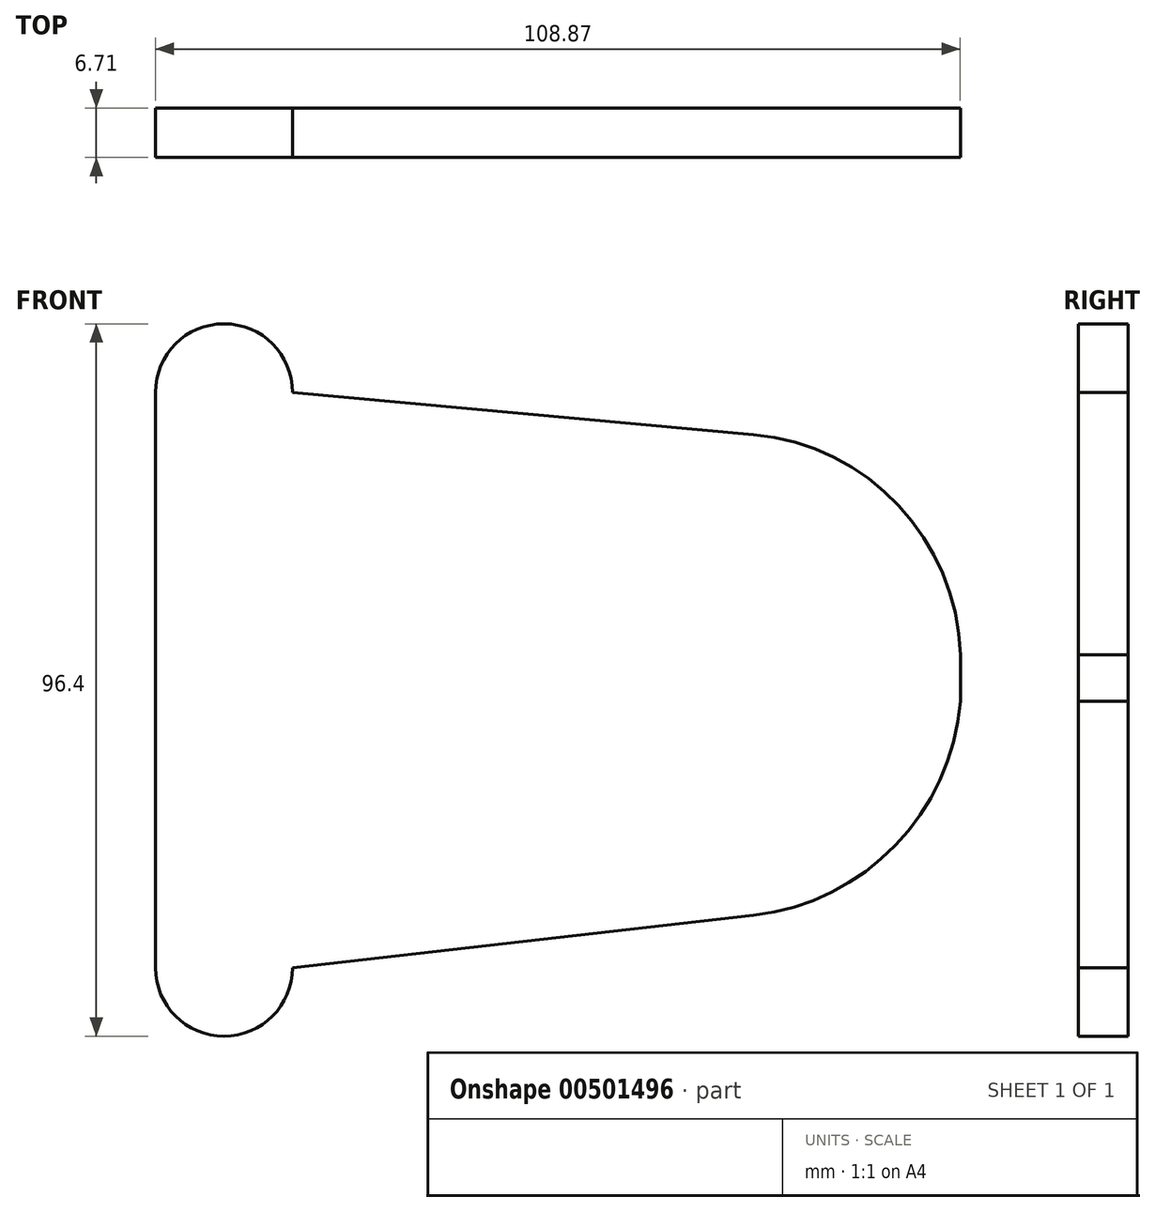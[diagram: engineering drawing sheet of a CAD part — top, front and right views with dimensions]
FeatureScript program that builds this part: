
annotation { "Feature Type Name" : "Feature", "Feature Type Description" : "" }
export const myFeature = defineFeature(function(context is Context, id is Id, definition is map)
    precondition{}
    {
        {
            var Q0;
            Q0=qCreatedBy(makeId("Front.planeOp"),FACE);
            var sketch = newSketch(context, id + "F0", { "sketchPlane" : qUnion([Q0])});
            skLineSegment(sketch, "E0.left", {"start": v(-50.55, 38.87) * mm, "end": v(-50.55, -39) * mm});
            skLineSegment(sketch, "E1", {"start": v(-32, -39) * mm, "end": v(30.35, -31.92) * mm});
            skLineSegment(sketch, "E2", {"start": v(-32, 38.87) * mm, "end": v(30.35, 33.14) * mm});
            skArc(sketch, "E3", {"start": v(-32, 38.87) * mm, "mid": v(-41.28, 48.14) * mm, "end": v(-50.55, 38.87) * mm});
            skArc(sketch, "E4", {"start": v(-32, -39) * mm, "mid": v(-41.28, -48.26) * mm, "end": v(-50.55, -39) * mm});
            skArc(sketch, "E5", {"start": v(30.35, 33.14) * mm, "mid": v(50, 23.54) * mm, "end": v(58.32, 3.34) * mm});
            skArc(sketch, "E6", {"start": v(30.35, -31.92) * mm, "mid": v(49.53, -22.47) * mm, "end": v(58.32, -2.97) * mm});
            skLineSegment(sketch, "E7", {"start": v(58.32, -2.97) * mm, "end": v(58.32, 3.34) * mm});
            skSolve(sketch);
        }
        {
            var Q0;
            Q0=makeQuery(id+"F0.imprint","IMPRINT",FACE,{"disambiguationData":[TD([[makeQuery(id+"F0.imprint","IMPRINT",EDGE,{"derivedFrom":sQuery(id+"F0.wireOp",EDGE,"E0.left")}),1.0]])]});
            extrude(context, id + "F1", {"entities" : qUnion([Q0]), "depth" : 6.7 * mm});
        }
        {
            var Q0;
            Q0=qCreatedBy(makeId("Front.planeOp"),FACE);
            var sketch = newSketch(context, id + "F2", { "sketchPlane" : qUnion([Q0])});
            skCircle(sketch, "E8", {"center": v(-39.08, 28.93) * mm, "radius": 6.72 * mm});
            skCircle(sketch, "E9", {"center": v(-39.08, -27.54) * mm, "radius": 6.72 * mm});
            skSolve(sketch);
        }
        {
            var Q0;
            Q0=sQuery(id+"F2.wireOp",EDGE,"E8");
            var Q1;
            Q1=sQuery(id+"F2.wireOp",EDGE,"E9");
            extrude(context, id + "F3", {"bodyType" : ToolBodyType.SURFACE, "surfaceEntities" : qUnion([Q0, Q1]), "depth" : 30.48 * mm});
        }
        {
            var Q0;
            Q0=qCreatedBy(makeId("Front.planeOp"),FACE);
            var sketch = newSketch(context, id + "F4", { "sketchPlane" : qUnion([Q0])});
            skLineSegment(sketch, "E10.bottom", {"start": v(15.26, 20.7) * mm, "end": v(41.8, 20.7) * mm});
            skLineSegment(sketch, "E10.top", {"start": v(15.26, -17.17) * mm, "end": v(41.8, -17.17) * mm});
            skLineSegment(sketch, "E10.left", {"start": v(15.26, 20.7) * mm, "end": v(15.26, -17.17) * mm});
            skLineSegment(sketch, "E10.right", {"start": v(41.8, 20.7) * mm, "end": v(41.8, -17.17) * mm});
            skSolve(sketch);
        }
        {
            var Q0;
            Q0=sQuery(id+"F4.wireOp",EDGE,"E10.right");
            var Q1;
            Q1=sQuery(id+"F4.wireOp",EDGE,"E10.left");
            var Q2;
            Q2=sQuery(id+"F4.wireOp",EDGE,"E10.top");
            var Q3;
            Q3=sQuery(id+"F4.wireOp",EDGE,"E10.bottom");
            extrude(context, id + "F5", {"bodyType" : ToolBodyType.SURFACE, "surfaceEntities" : qUnion([Q0, Q1, Q2, Q3]), "oppositeDirection" : true, "depth" : 22.25 * mm});
        }
    });
